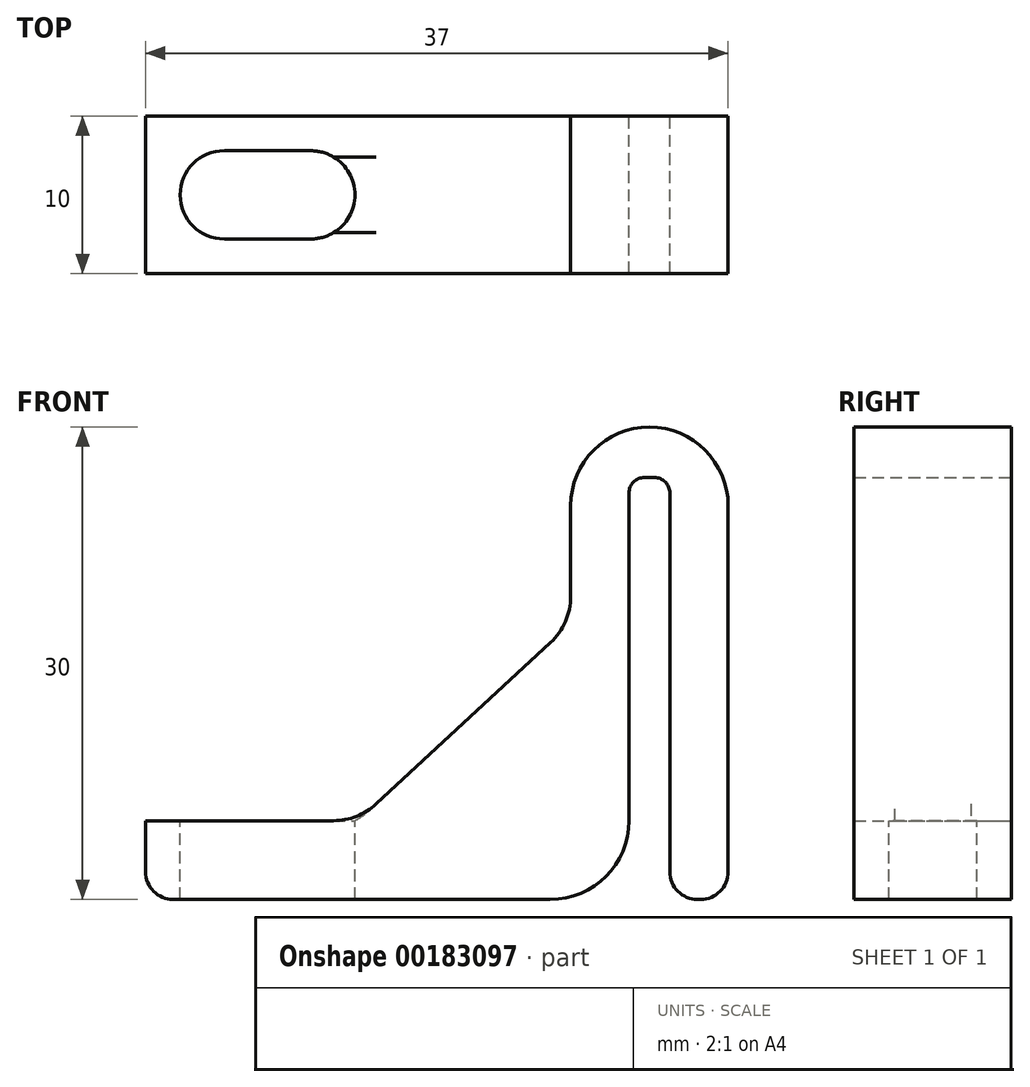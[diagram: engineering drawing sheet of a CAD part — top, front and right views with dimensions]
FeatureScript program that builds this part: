
annotation { "Feature Type Name" : "Feature", "Feature Type Description" : "" }
export const myFeature = defineFeature(function(context is Context, id is Id, definition is map)
    precondition{}
    {
        {
            var Q0;
            Q0=qCreatedBy(makeId("Front.planeOp"),FACE);
            var sketch = newSketch(context, id + "F0", { "sketchPlane" : qUnion([Q0])});
            skLineSegment(sketch, "E0", {"start": v(0, 0) * mm, "end": v(0, 15) * mm});
            skLineSegment(sketch, "E1", {"start": v(0, 15) * mm, "end": v(-10, 15) * mm});
            skLineSegment(sketch, "E2", {"start": v(-10, 15) * mm, "end": v(-10, -10) * mm});
            skLineSegment(sketch, "E3", {"start": v(-10, -10) * mm, "end": v(-37, -10) * mm});
            skLineSegment(sketch, "E4", {"start": v(-37, -10) * mm, "end": v(-37, -15) * mm});
            skLineSegment(sketch, "E5", {"start": v(-37, -15) * mm, "end": v(0, -15) * mm});
            skLineSegment(sketch, "E6", {"start": v(0, -15) * mm, "end": v(0, 0) * mm});
            skLineSegment(sketch, "E7", {"start": v(-5, 15) * mm, "end": v(-5, -15) * mm});
            skLineSegment(sketch, "E8", {"start": v(-5, 15) * mm, "end": v(-5, 11.8) * mm});
            skLineSegment(sketch, "E9", {"start": v(-5, 11.8) * mm, "end": v(-6.3, 11.8) * mm});
            skLineSegment(sketch, "E10", {"start": v(-6.3, 11.8) * mm, "end": v(-6.3, -15) * mm});
            skLineSegment(sketch, "E11.MirrorCS", {"start": v(-5, 11.8) * mm, "end": v(-3.7, 11.8) * mm});
            skLineSegment(sketch, "E12.MirrorCS", {"start": v(-3.7, 11.8) * mm, "end": v(-3.7, -15) * mm});
            skLineSegment(sketch, "E13", {"start": v(-23.5, -10) * mm, "end": v(-10, 2.5) * mm});
            skSolve(sketch);
        }
        {
            var Q0;
            {var subQ4=sQuery(id+"F0.wireOp",EDGE,"E0");Q0=makeQuery(id+"F0.imprint","IMPRINT",FACE,{"disambiguationData":[TD([[makeQuery(id+"F0.imprint","IMPRINT",EDGE,{"derivedFrom":subQ4}),1.0]])]});}
            var Q1;
            {var subQ2=sQuery(id+"F0.wireOp",EDGE,"E2");Q1=makeQuery(id+"F0.imprint","IMPRINT",FACE,{"disambiguationData":[TD([[makeQuery(id+"F0.imprint","IMPRINT",EDGE,{"derivedFrom":subQ2}),1.0]])]});}
            var Q2;
            {var subQ3=sQuery(id+"F0.wireOp",EDGE,"E13");Q2=makeQuery(id+"F0.imprint","IMPRINT",FACE,{"disambiguationData":[TD([[makeQuery(id+"F0.imprint","IMPRINT",EDGE,{"derivedFrom":subQ3}),-1.0]])]});}
            extrude(context, id + "F1", {"entities" : qUnion([Q0, Q1, Q2]), "depth" : 10 * mm});
        }
        {
            var Q0;
            Q0=makeQuery(id+"F1.opExtrude","SWEPT_FACE",FACE,{"disambiguationData":[OSD([sQuery(id+"F0.wireOp",EDGE,"E3")])]});
            var sketch = newSketch(context, id + "F2", { "sketchPlane" : qUnion([Q0])});
            skLineSegment(sketch, "E14", {"start": v(-37, -5) * mm, "end": v(-32, -5) * mm});
            skCircle(sketch, "E15", {"center": v(-32, -5) * mm, "radius": 2.8 * mm});
            skLineSegment(sketch, "E16", {"start": v(-32, -5) * mm, "end": v(-26.5, -5) * mm});
            skCircle(sketch, "E17", {"center": v(-26.5, -5) * mm, "radius": 2.8 * mm});
            skLineSegment(sketch, "E18", {"start": v(-32, -2.2) * mm, "end": v(-26.5, -2.2) * mm});
            skLineSegment(sketch, "E19", {"start": v(-32, -7.8) * mm, "end": v(-26.5, -7.8) * mm});
            skSolve(sketch);
        }
        {
            var Q0;
            Q0=makeQuery(id+"F1.opExtrude","SWEPT_EDGE",EDGE,{"disambiguationData":[OSD([sQuery(id+"F0.wireOp",EDGE,"E1"),sQuery(id+"F0.wireOp",EDGE,"E2")])]});
            var Q1;
            Q1=makeQuery(id+"F1.opExtrude","SWEPT_EDGE",EDGE,{"disambiguationData":[OSD([sQuery(id+"F0.wireOp",EDGE,"E0"),sQuery(id+"F0.wireOp",EDGE,"E1")])]});
            var Q2;
            Q2=makeQuery(id+"F1.opExtrude","SWEPT_EDGE",EDGE,{"disambiguationData":[OSD([sQuery(id+"F0.wireOp",EDGE,"E5"),sQuery(id+"F0.wireOp",EDGE,"E10")])]});
            fillet(context, id + "F3", {"entities" : qUnion([Q0, Q1, Q2]), "radius" : 5 * mm, "tangentPropagation" : true, "allowEdgeOverflow" : false});
        }
        {
            var Q0;
            Q0=makeQuery(id+"F2.imprint","IMPRINT",FACE,{"disambiguationData":[TD([[makeQuery(id+"F2.imprint","IMPRINT",EDGE,{"derivedFrom":sQuery(id+"F2.wireOp",EDGE,"E15")}),1.0]])]});
            var Q1;
            {var subQ0=sQuery(id+"F2.wireOp",EDGE,"E17");var subQ1=makeQuery(id+"F2.imprint","INTERSECT",VERTEX,{"derivedFrom":[subQ0,sQuery(id+"F2.wireOp",EDGE,"E18")]});Q1=makeQuery(id+"F2.imprint","IMPRINT",FACE,{"disambiguationData":[TD([[makeQuery(id+"F2.imprint","IMPRINT",EDGE,{"disambiguationData":[TD([[subQ1,-1.0]])],"derivedFrom":subQ0}),1.0]])]});}
            var Q2;
            {var subQ0=sQuery(id+"F2.wireOp",EDGE,"E18");Q2=makeQuery(id+"F2.imprint","IMPRINT",FACE,{"disambiguationData":[TD([[makeQuery(id+"F2.imprint","IMPRINT",EDGE,{"derivedFrom":subQ0}),-1.0]])]});}
            var Q3;
            {var subQ0=sQuery(id+"F2.wireOp",EDGE,"E19");Q3=makeQuery(id+"F2.imprint","IMPRINT",FACE,{"disambiguationData":[TD([[makeQuery(id+"F2.imprint","IMPRINT",EDGE,{"derivedFrom":subQ0}),1.0]])]});}
            var Q4;
            {var subQ0=sQuery(id+"F2.wireOp",EDGE,"E16");var subQ1=sQuery(id+"F2.wireOp",EDGE,"E15");var subQ2=makeQuery(id+"F2.imprint","INTERSECT",VERTEX,{"derivedFrom":[subQ1,subQ0]});Q4=makeQuery(id+"F2.imprint","IMPRINT",FACE,{"disambiguationData":[TD([[makeQuery(id+"F2.imprint","IMPRINT",EDGE,{"disambiguationData":[TD([[subQ2,-1.0]])],"derivedFrom":subQ1}),1.0]])]});}
            var Q5;
            {var subQ0=sQuery(id+"F2.wireOp",EDGE,"E16");var subQ1=sQuery(id+"F2.wireOp",EDGE,"E15");var subQ2=makeQuery(id+"F2.imprint","INTERSECT",VERTEX,{"derivedFrom":[subQ1,subQ0]});Q5=makeQuery(id+"F2.imprint","IMPRINT",FACE,{"disambiguationData":[TD([[makeQuery(id+"F2.imprint","IMPRINT",EDGE,{"disambiguationData":[TD([[subQ2,1.0]])],"derivedFrom":subQ1}),1.0]])]});}
            extrude(context, id + "F4", {"entities" : qUnion([Q0, Q1, Q2, Q3, Q4, Q5]), "operationType" : NewBodyOperationType.REMOVE, "oppositeDirection" : true, "depth" : 25 * mm});
        }
        {
            var Q0;
            Q0=makeQuery(id+"F1.opExtrude","SWEPT_EDGE",EDGE,{"disambiguationData":[OSD([sQuery(id+"F0.wireOp",EDGE,"E4"),sQuery(id+"F0.wireOp",EDGE,"E5")])]});
            var Q1;
            Q1=makeQuery(id+"F1.opExtrude","SWEPT_EDGE",EDGE,{"disambiguationData":[OSD([sQuery(id+"F0.wireOp",EDGE,"E5"),sQuery(id+"F0.wireOp",EDGE,"E12.MirrorCS")])]});
            var Q2;
            Q2=makeQuery(id+"F1.opExtrude","SWEPT_EDGE",EDGE,{"disambiguationData":[OSD([sQuery(id+"F0.wireOp",EDGE,"E5"),sQuery(id+"F0.wireOp",EDGE,"E6")])]});
            fillet(context, id + "F5", {"entities" : qUnion([Q0, Q1, Q2]), "radius" : 1.75 * mm, "tangentPropagation" : true, "allowEdgeOverflow" : false});
        }
        {
            var Q0;
            Q0=makeQuery(id+"F1.opExtrude","SWEPT_EDGE",EDGE,{"disambiguationData":[OSD([sQuery(id+"F0.wireOp",EDGE,"E2"),sQuery(id+"F0.wireOp",EDGE,"E13")])]});
            var Q1;
            Q1=makeQuery(id+"F1.opExtrude","SWEPT_EDGE",EDGE,{"disambiguationData":[OSD([sQuery(id+"F0.wireOp",EDGE,"E3"),sQuery(id+"F0.wireOp",EDGE,"E13")])]});
            fillet(context, id + "F6", {"entities" : qUnion([Q0, Q1]), "radius" : 4 * mm, "tangentPropagation" : true, "allowEdgeOverflow" : false});
        }
        {
            var Q0;
            Q0=makeQuery(id+"F1.opExtrude","SWEPT_EDGE",EDGE,{"disambiguationData":[OSD([sQuery(id+"F0.wireOp",EDGE,"E11.MirrorCS"),sQuery(id+"F0.wireOp",EDGE,"E12.MirrorCS")])]});
            var Q1;
            Q1=makeQuery(id+"F1.opExtrude","SWEPT_EDGE",EDGE,{"disambiguationData":[OSD([sQuery(id+"F0.wireOp",EDGE,"E9"),sQuery(id+"F0.wireOp",EDGE,"E10")])]});
            fillet(context, id + "F7", {"entities" : qUnion([Q0, Q1]), "radius" : 1 * mm, "tangentPropagation" : true, "allowEdgeOverflow" : false});
        }
    });
